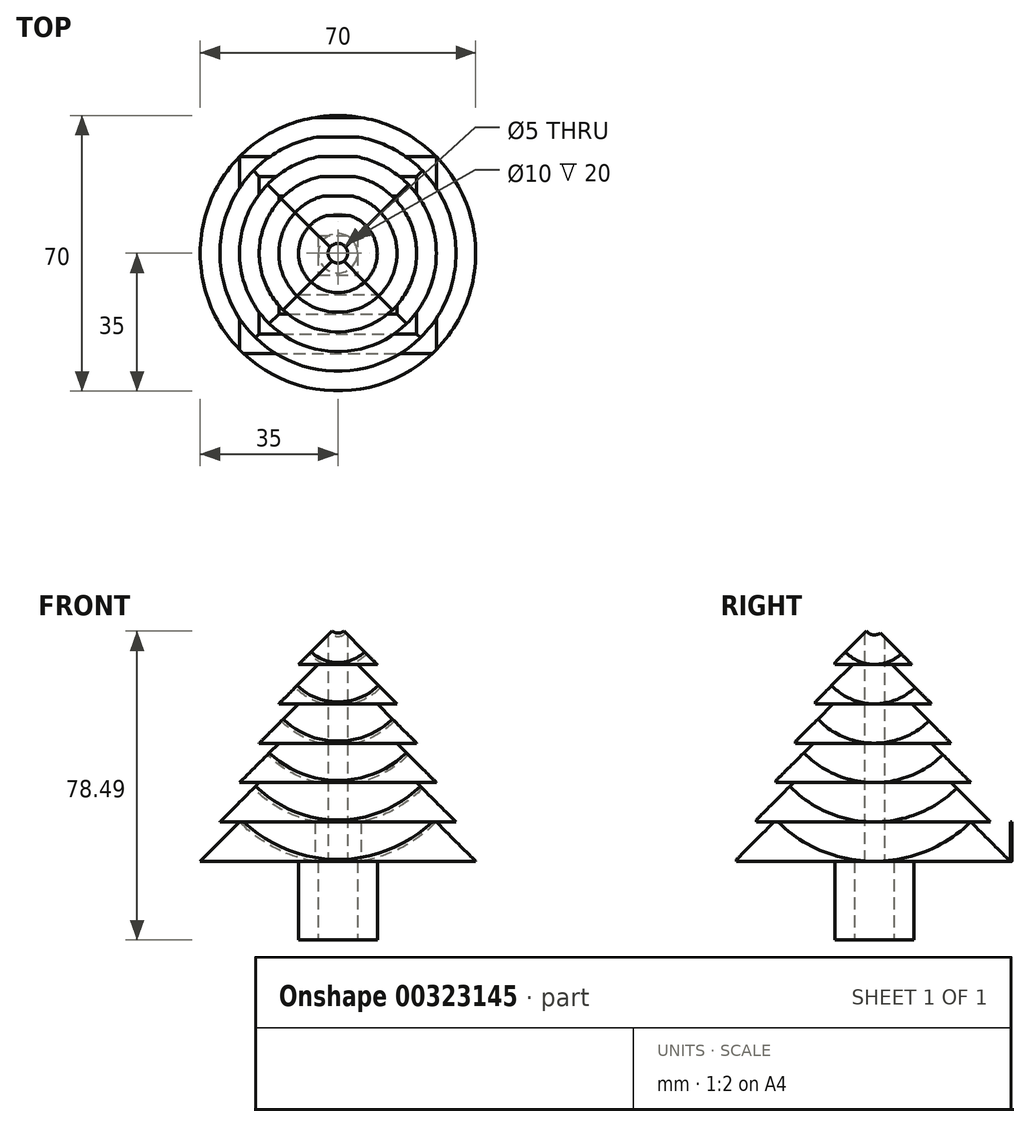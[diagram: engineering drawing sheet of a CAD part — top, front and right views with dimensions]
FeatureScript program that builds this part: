
annotation { "Feature Type Name" : "Feature", "Feature Type Description" : "" }
export const myFeature = defineFeature(function(context is Context, id is Id, definition is map)
    precondition{}
    {
        {
            var Q0;
            Q0=qCreatedBy(makeId("Top.planeOp"),FACE);
            var sketch = newSketch(context, id + "F0", { "sketchPlane" : qUnion([Q0])});
            skCircle(sketch, "E0", {"center": v(0, 0) * mm, "radius": 15 * mm});
            skCircle(sketch, "E1", {"center": v(0, 0) * mm, "radius": 10 * mm});
            skCircle(sketch, "E2", {"center": v(0, 0) * mm, "radius": 20 * mm});
            skCircle(sketch, "E3", {"center": v(0, 0) * mm, "radius": 25 * mm});
            skCircle(sketch, "E4", {"center": v(0, 0) * mm, "radius": 30 * mm});
            skCircle(sketch, "E5", {"center": v(0, 0) * mm, "radius": 35 * mm});
            skCircle(sketch, "E6", {"center": v(0, 0) * mm, "radius": 5 * mm});
            skCircle(sketch, "E7", {"center": v(0, 0) * mm, "radius": 2.5 * mm});
            skSolve(sketch);
        }
        {
            var Q0;
            Q0 = qSketchRegion(id + "F0", true);
            extrude(context, id + "F1", {"entities" : qUnion([Q0]), "depth" : 10 * mm});
        }
        {
            var Q0;
            Q0=makeQuery(id+"F0.imprint","IMPRINT",FACE,{"disambiguationData":[TD([[makeQuery(id+"F0.imprint","IMPRINT",EDGE,{"derivedFrom":sQuery(id+"F0.wireOp",EDGE,"E3")}),-1.0]])]});
            extrude(context, id + "F2", {"entities" : qUnion([Q0]), "operationType" : NewBodyOperationType.ADD, "depth" : 20 * mm});
        }
        {
            var Q0;
            Q0=makeQuery(id+"F0.imprint","IMPRINT",FACE,{"disambiguationData":[TD([[makeQuery(id+"F0.imprint","IMPRINT",EDGE,{"derivedFrom":sQuery(id+"F0.wireOp",EDGE,"E2")}),-1.0]])]});
            extrude(context, id + "F3", {"entities" : qUnion([Q0]), "operationType" : NewBodyOperationType.ADD, "depth" : 30 * mm});
        }
        {
            var Q0;
            Q0=makeQuery(id+"F0.imprint","IMPRINT",FACE,{"disambiguationData":[TD([[makeQuery(id+"F0.imprint","IMPRINT",EDGE,{"derivedFrom":sQuery(id+"F0.wireOp",EDGE,"E0")}),-1.0]])]});
            extrude(context, id + "F4", {"entities" : qUnion([Q0]), "operationType" : NewBodyOperationType.ADD, "depth" : 40 * mm});
        }
        {
            var Q0;
            Q0=makeQuery(id+"F0.imprint","IMPRINT",FACE,{"disambiguationData":[TD([[makeQuery(id+"F0.imprint","IMPRINT",EDGE,{"derivedFrom":sQuery(id+"F0.wireOp",EDGE,"E0")}),1.0]])]});
            extrude(context, id + "F5", {"entities" : qUnion([Q0]), "operationType" : NewBodyOperationType.ADD, "depth" : 50 * mm});
        }
        {
            var Q0;
            Q0=makeQuery(id+"F0.imprint","IMPRINT",FACE,{"disambiguationData":[TD([[makeQuery(id+"F0.imprint","IMPRINT",EDGE,{"derivedFrom":sQuery(id+"F0.wireOp",EDGE,"E1")}),1.0]])]});
            extrude(context, id + "F6", {"entities" : qUnion([Q0]), "operationType" : NewBodyOperationType.ADD, "depth" : 60 * mm, "hasSecondDirection" : true, "secondDirectionOppositeDirection" : true, "secondDirectionDepth" : 20 * mm});
        }
        {
            var Q0;
            Q0=makeQuery(id+"F0.imprint","IMPRINT",FACE,{"disambiguationData":[TD([[makeQuery(id+"F0.imprint","IMPRINT",EDGE,{"derivedFrom":sQuery(id+"F0.wireOp",EDGE,"E6")}),1.0]])]});
            extrude(context, id + "F7", {"entities" : qUnion([Q0]), "operationType" : NewBodyOperationType.ADD, "depth" : 60 * mm});
        }
        {
            var Q0;
            Q0=qCreatedBy(makeId("Front.planeOp"),FACE);
            var sketch = newSketch(context, id + "F8", { "sketchPlane" : qUnion([Q0])});
            skLineSegment(sketch, "E8", {"start": v(-35, 0) * mm, "end": v(-25, 10) * mm});
            skLineSegment(sketch, "E9", {"start": v(-30, 10) * mm, "end": v(-25, 10) * mm});
            skLineSegment(sketch, "E10", {"start": v(-30, 10) * mm, "end": v(-20, 20) * mm});
            skLineSegment(sketch, "E11", {"start": v(-25, 20) * mm, "end": v(-20, 20) * mm});
            skLineSegment(sketch, "E12", {"start": v(-25, 20) * mm, "end": v(-15, 30) * mm});
            skLineSegment(sketch, "E13", {"start": v(-20, 30) * mm, "end": v(-15, 30) * mm});
            skLineSegment(sketch, "E14", {"start": v(-20, 30) * mm, "end": v(-10, 40) * mm});
            skLineSegment(sketch, "E15", {"start": v(-15, 40) * mm, "end": v(-10, 40) * mm});
            skLineSegment(sketch, "E16", {"start": v(-15, 40) * mm, "end": v(-5, 50) * mm});
            skLineSegment(sketch, "E17", {"start": v(-10, 50) * mm, "end": v(-5, 50) * mm});
            skLineSegment(sketch, "E18", {"start": v(-10, 50) * mm, "end": v(0, 60) * mm});
            skLineSegment(sketch, "E19", {"start": v(-5, 60) * mm, "end": v(0, 60) * mm});
            skLineSegment(sketch, "E20.MirrorCS", {"start": v(25, 20) * mm, "end": v(20, 20) * mm});
            skLineSegment(sketch, "E21.MirrorCS", {"start": v(20, 30) * mm, "end": v(15, 30) * mm});
            skLineSegment(sketch, "E22.MirrorCS", {"start": v(15, 40) * mm, "end": v(10, 40) * mm});
            skLineSegment(sketch, "E23.MirrorCS", {"start": v(10, 50) * mm, "end": v(5, 50) * mm});
            skLineSegment(sketch, "E24.MirrorCS", {"start": v(30, 10) * mm, "end": v(25, 10) * mm});
            skLineSegment(sketch, "E25.MirrorCS", {"start": v(5, 60) * mm, "end": v(0, 60) * mm});
            skLineSegment(sketch, "E26.MirrorCS", {"start": v(35, 0) * mm, "end": v(25, 10) * mm});
            skLineSegment(sketch, "E27.MirrorCS", {"start": v(20, 30) * mm, "end": v(10, 40) * mm});
            skLineSegment(sketch, "E28.MirrorCS", {"start": v(15, 40) * mm, "end": v(5, 50) * mm});
            skLineSegment(sketch, "E29.MirrorCS", {"start": v(10, 50) * mm, "end": v(0, 60) * mm});
            skLineSegment(sketch, "E30.MirrorCS", {"start": v(30, 10) * mm, "end": v(20, 20) * mm});
            skLineSegment(sketch, "E31.MirrorCS", {"start": v(25, 20) * mm, "end": v(15, 30) * mm});
            skLineSegment(sketch, "E32", {"start": v(-35, 0) * mm, "end": v(-35, 60) * mm});
            skLineSegment(sketch, "E33", {"start": v(-35, 60) * mm, "end": v(0, 60) * mm});
            skLineSegment(sketch, "E34", {"start": v(35, 0) * mm, "end": v(35, 60) * mm});
            skLineSegment(sketch, "E35", {"start": v(35, 60) * mm, "end": v(0, 60) * mm});
            skSolve(sketch);
        }
        {
            var Q0;
            Q0=makeQuery(id+"F8.imprint","IMPRINT",FACE,{"disambiguationData":[TD([[makeQuery(id+"F8.imprint","IMPRINT",EDGE,{"derivedFrom":sQuery(id+"F8.wireOp",EDGE,"E8")}),1.0]])]});
            var Q1;
            Q1=makeQuery(id+"F8.imprint","IMPRINT",FACE,{"disambiguationData":[TD([[makeQuery(id+"F8.imprint","IMPRINT",EDGE,{"derivedFrom":sQuery(id+"F8.wireOp",EDGE,"E20.MirrorCS")}),1.0]])]});
            extrude(context, id + "F9", {"entities" : qUnion([Q0, Q1]), "operationType" : NewBodyOperationType.REMOVE, "oppositeDirection" : true, "depth" : 100 * mm, "hasSecondDirection" : true, "secondDirectionOppositeDirection" : false, "secondDirectionDepth" : 100 * mm});
        }
        {
            var Q0;
            Q0=qCreatedBy(makeId("Right.planeOp"),FACE);
            var sketch = newSketch(context, id + "F10", { "sketchPlane" : qUnion([Q0])});
            skLineSegment(sketch, "E36", {"start": v(-35.49, 0) * mm, "end": v(-25.49, 10) * mm});
            skLineSegment(sketch, "E37", {"start": v(-30.49, 10) * mm, "end": v(-25.49, 10) * mm});
            skLineSegment(sketch, "E38", {"start": v(-30.49, 10) * mm, "end": v(-20.49, 20) * mm});
            skLineSegment(sketch, "E39", {"start": v(-25.49, 20) * mm, "end": v(-20.49, 20) * mm});
            skLineSegment(sketch, "E40", {"start": v(-25.49, 20) * mm, "end": v(-15.49, 30) * mm});
            skLineSegment(sketch, "E41", {"start": v(-20.49, 30) * mm, "end": v(-15.49, 30) * mm});
            skLineSegment(sketch, "E42", {"start": v(-20.49, 30) * mm, "end": v(-10.49, 40) * mm});
            skLineSegment(sketch, "E43", {"start": v(-15.49, 40) * mm, "end": v(-10.49, 40) * mm});
            skLineSegment(sketch, "E44", {"start": v(-15.49, 40) * mm, "end": v(-5.49, 50) * mm});
            skLineSegment(sketch, "E45", {"start": v(-10.49, 50) * mm, "end": v(-5.49, 50) * mm});
            skLineSegment(sketch, "E46", {"start": v(-10.49, 50) * mm, "end": v(-0.49, 60) * mm});
            skLineSegment(sketch, "E47", {"start": v(-5.49, 60) * mm, "end": v(-0.49, 60) * mm});
            skLineSegment(sketch, "E48.MirrorCS", {"start": v(24.51, 20) * mm, "end": v(19.51, 20) * mm});
            skLineSegment(sketch, "E49.MirrorCS", {"start": v(19.51, 30) * mm, "end": v(14.51, 30) * mm});
            skLineSegment(sketch, "E50.MirrorCS", {"start": v(14.51, 40) * mm, "end": v(9.51, 40) * mm});
            skLineSegment(sketch, "E51.MirrorCS", {"start": v(9.51, 50) * mm, "end": v(4.51, 50) * mm});
            skLineSegment(sketch, "E52.MirrorCS", {"start": v(29.51, 10) * mm, "end": v(24.51, 10) * mm});
            skLineSegment(sketch, "E53.MirrorCS", {"start": v(4.51, 60) * mm, "end": v(-0.49, 60) * mm});
            skLineSegment(sketch, "E54.MirrorCS", {"start": v(34.51, 0) * mm, "end": v(24.51, 10) * mm});
            skLineSegment(sketch, "E55.MirrorCS", {"start": v(19.51, 30) * mm, "end": v(9.51, 40) * mm});
            skLineSegment(sketch, "E56.MirrorCS", {"start": v(14.51, 40) * mm, "end": v(4.51, 50) * mm});
            skLineSegment(sketch, "E57.MirrorCS", {"start": v(9.51, 50) * mm, "end": v(-0.49, 60) * mm});
            skLineSegment(sketch, "E58.MirrorCS", {"start": v(29.51, 10) * mm, "end": v(19.51, 20) * mm});
            skLineSegment(sketch, "E59.MirrorCS", {"start": v(24.51, 20) * mm, "end": v(14.51, 30) * mm});
            skLineSegment(sketch, "E60", {"start": v(-35.49, 0) * mm, "end": v(-35.49, 60) * mm});
            skLineSegment(sketch, "E61", {"start": v(-35.49, 60) * mm, "end": v(-0.49, 60) * mm});
            skLineSegment(sketch, "E62", {"start": v(34.51, 0) * mm, "end": v(34.51, 60) * mm});
            skLineSegment(sketch, "E63", {"start": v(34.51, 60) * mm, "end": v(-0.49, 60) * mm});
            skSolve(sketch);
        }
        {
            var Q0;
            Q0 = qSketchRegion(id + "F10", true);
            extrude(context, id + "F11", {"entities" : qUnion([Q0]), "operationType" : NewBodyOperationType.REMOVE, "oppositeDirection" : true, "depth" : 100 * mm, "hasSecondDirection" : true, "secondDirectionOppositeDirection" : false, "secondDirectionDepth" : 100 * mm});
        }
    });
